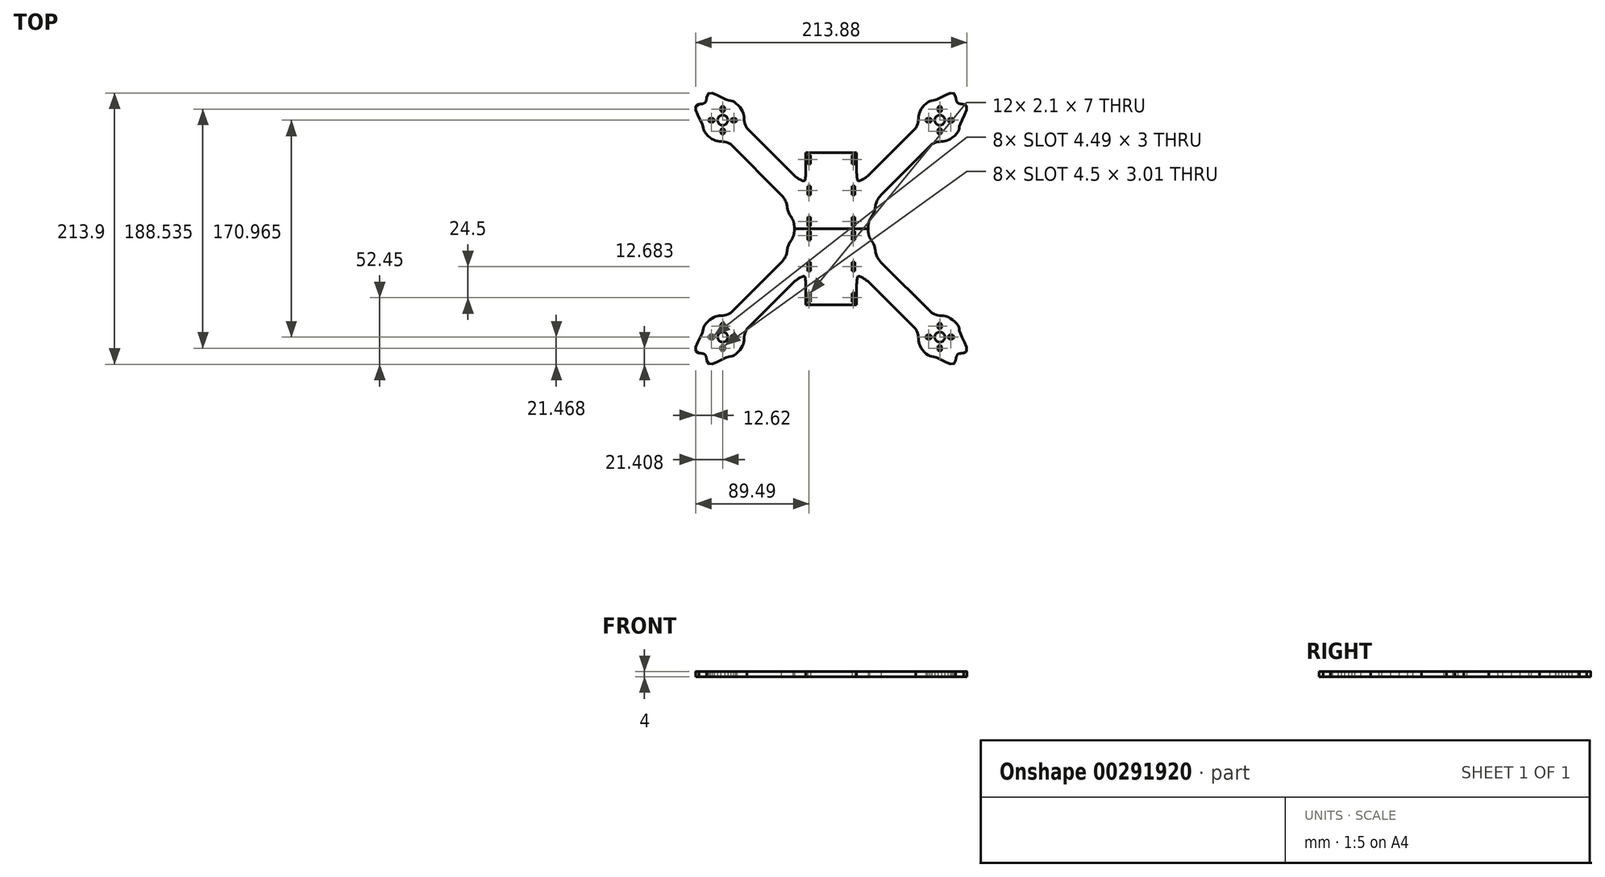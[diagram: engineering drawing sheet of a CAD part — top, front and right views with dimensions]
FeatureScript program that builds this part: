
annotation { "Feature Type Name" : "Feature", "Feature Type Description" : "" }
export const myFeature = defineFeature(function(context is Context, id is Id, definition is map)
    precondition{}
    {
        {
            var Q0;
            Q0=qCreatedBy(makeId("Top.planeOp"),FACE);
            var sketch = newSketch(context, id + "F0", { "sketchPlane" : qUnion([Q0])});
            skCircle(sketch, "E0", {"center": v(-85.5, 85.52) * mm, "radius": 4 * mm});
            skArc(sketch, "E1", {"start": v(-75.8, 84) * mm, "mid": v(-74.5, 85.58) * mm, "end": v(-76.01, 86.98) * mm});
            skLineSegment(sketch, "E2", {"start": v(-76.01, 86.98) * mm, "end": v(-77.51, 86.97) * mm});
            skLineSegment(sketch, "E3", {"start": v(-75.8, 84) * mm, "end": v(-77.3, 83.98) * mm});
            skArc(sketch, "E4", {"start": v(-77.51, 86.97) * mm, "mid": v(-79, 85.37) * mm, "end": v(-77.3, 83.98) * mm});
            skLineSegment(sketch, "E5", {"start": v(-85.53, 85.52) * mm, "end": v(-85.53, 96.52) * mm, "construction": true});
            skLineSegment(sketch, "E6", {"start": v(-85.5, 85.52) * mm, "end": v(-85.46, 74.52) * mm, "construction": true});
            skLineSegment(sketch, "E7.MirrorCS", {"start": v(-95.26, 84) * mm, "end": v(-93.76, 83.98) * mm});
            skLineSegment(sketch, "E8.MirrorCS", {"start": v(-95.06, 86.98) * mm, "end": v(-93.56, 86.97) * mm});
            skArc(sketch, "E9.MirrorCS", {"start": v(-93.56, 86.97) * mm, "mid": v(-92.07, 85.37) * mm, "end": v(-93.76, 83.98) * mm});
            skArc(sketch, "E10.MirrorCS", {"start": v(-95.26, 84) * mm, "mid": v(-96.57, 85.58) * mm, "end": v(-95.06, 86.98) * mm});
            skLineSegment(sketch, "E11", {"start": v(-96.57, 85.48) * mm, "end": v(-74.5, 85.56) * mm, "construction": true});
            skLineSegment(sketch, "E12.MirrorCS", {"start": v(-86.97, 77.51) * mm, "end": v(-86.97, 76.01) * mm});
            skLineSegment(sketch, "E13.MirrorCS", {"start": v(-83.97, 77.52) * mm, "end": v(-83.97, 76.02) * mm});
            skArc(sketch, "E14.MirrorCS", {"start": v(-83.97, 76.02) * mm, "mid": v(-85.46, 74.52) * mm, "end": v(-86.97, 76.01) * mm});
            skArc(sketch, "E15.MirrorCS", {"start": v(-86.97, 77.51) * mm, "mid": v(-85.48, 79.02) * mm, "end": v(-83.97, 77.52) * mm});
            skArc(sketch, "E16.MirrorCS", {"start": v(-87.03, 93.51) * mm, "mid": v(-85.52, 92.02) * mm, "end": v(-84.03, 93.52) * mm});
            skLineSegment(sketch, "E17.MirrorCS", {"start": v(-84.03, 93.52) * mm, "end": v(-84.03, 95.02) * mm});
            skLineSegment(sketch, "E18.MirrorCS", {"start": v(-87.03, 93.51) * mm, "end": v(-87.03, 95.01) * mm});
            skArc(sketch, "E19.MirrorCS", {"start": v(-84.03, 95.02) * mm, "mid": v(-85.54, 96.52) * mm, "end": v(-87.03, 95.01) * mm});
            skLineSegment(sketch, "E20", {"start": v(-85.5, 85.52) * mm, "end": v(-95.4, 95.42) * mm, "construction": true});
            skLineSegment(sketch, "E21", {"start": v(-85.53, 96.52) * mm, "end": v(-85.53, 99.52) * mm, "construction": true});
            skLineSegment(sketch, "E22", {"start": v(-96.57, 85.48) * mm, "end": v(-99.5, 85.48) * mm, "construction": true});
            skLineSegment(sketch, "E23", {"start": v(-85.46, 74.52) * mm, "end": v(-85.46, 71.52) * mm, "construction": true});
            skLineSegment(sketch, "E24", {"start": v(-85.5, 85.52) * mm, "end": v(-75.6, 95.42) * mm, "construction": true});
            skLineSegment(sketch, "E25", {"start": v(-85.5, 85.52) * mm, "end": v(-95.4, 75.62) * mm, "construction": true});
            skPoint(sketch, "E26", {"position": v(-56.32, 40.18) * mm});
            skLineSegment(sketch, "E27", {"start": v(-85.5, 85.52) * mm, "end": v(-75.6, 75.62) * mm, "construction": true});
            skCircle(sketch, "E28", {"center": v(-85.5, 85.52) * mm, "radius": 14 * mm, "construction": true});
            skLineSegment(sketch, "E29", {"start": v(-74.5, 85.56) * mm, "end": v(-71.5, 85.56) * mm, "construction": true});
            skPoint(sketch, "E30.visualSharp", {"position": v(-85.46, 71.52) * mm});
            skPoint(sketch, "E31.visualSharp", {"position": v(-71.5, 85.56) * mm});
            skLineSegment(sketch, "E32", {"start": v(-20, 60) * mm, "end": v(0, 60) * mm});
            skLineSegment(sketch, "E33", {"start": v(0, 60) * mm, "end": v(0, 0) * mm});
            skLineSegment(sketch, "E34", {"start": v(-85.5, 85.52) * mm, "end": v(-22, 85.52) * mm, "construction": true});
            skCircle(sketch, "E35", {"center": v(-85.5, 85.52) * mm, "radius": 63.5 * mm, "construction": true});
            skLineSegment(sketch, "E36", {"start": v(-29, -0.02) * mm, "end": v(-29, 0) * mm, "construction": true});
            skPoint(sketch, "E37.visualSharp", {"position": v(-86.14, 109.55) * mm});
            skPoint(sketch, "E38.visualSharp", {"position": v(-109.53, 84.88) * mm});
            skArc(sketch, "E39", {"start": v(-29, 0) * mm, "mid": v(-29.3, 3.46) * mm, "end": v(-30.18, 6.81) * mm});
            skLineSegment(sketch, "E40.trimOffspring", {"start": v(-20.02, -0.02) * mm, "end": v(-20, 0) * mm});
            skLineSegment(sketch, "E41", {"start": v(-66.5, 79.25) * mm, "end": v(-29.98, 42.73) * mm});
            skLineSegment(sketch, "E42", {"start": v(-79.23, 66.52) * mm, "end": v(-39.33, 26.61) * mm});
            skFitSpline(sketch, "E43", {"points": [v(-79.23, 66.52) * mm, v(-84.99, 68.53) * mm, v(-89.4, 68.97) * mm, v(-94.25, 70.94) * mm, v(-100.14, 76.88) * mm, v(-102.47, 84.44) * mm, v(-97.84, 97.21) * mm], "startDerivative": vector(-52.25, 30.78) * mm, "endDerivative": vector(200.56, -55.38) * mm});
            skFitSpline(sketch, "E44.MirrorCS", {"points": [v(-66.5, 79.25) * mm, v(-68.5, 85) * mm, v(-68.95, 89.42) * mm, v(-70.93, 94.27) * mm, v(-76.86, 100.16) * mm, v(-84.42, 102.48) * mm, v(-97.2, 97.85) * mm], "startDerivative": vector(-30.78, 52.25) * mm, "endDerivative": vector(55.38, -200.56) * mm});
            skFitSpline(sketch, "E45", {"points": [v(-39.33, 26.61) * mm, v(-33.76, 13.03) * mm, v(-29, 0) * mm], "startDerivative": vector(33.41, -38.03) * mm, "endDerivative": vector(-8.78, -30.15) * mm});
            skPoint(sketch, "E46.orphan", {"position": v(-104.03, 90.68) * mm});
            skPoint(sketch, "E37.filletArc.end.orphan", {"position": v(-91.65, 103.74) * mm});
            skPoint(sketch, "E47.end.orphan", {"position": v(-20, 46.85) * mm});
            skFitSpline(sketch, "E48", {"points": [v(-30.19, 42.93) * mm, v(-21.98, 37.6) * mm, v(-20, 44.2) * mm], "startDerivative": vector(14.75, -14.96) * mm, "endDerivative": vector(2.34, 37.6) * mm});
            skLineSegment(sketch, "E49.trimOffspring", {"start": v(-20, 44.2) * mm, "end": v(-20, 60) * mm});
            skFitSpline(sketch, "E50", {"points": [v(-98.1, 103.81) * mm, v(-99.54, 99.28) * mm, v(-104.27, 98.07) * mm], "startDerivative": vector(-1.03, -9.76) * mm, "endDerivative": vector(-11.13, -1.87) * mm});
            skLineSegment(sketch, "E51", {"start": v(-29, 0) * mm, "end": v(0, 0) * mm});
            skLineSegment(sketch, "E52.bottom", {"start": v(-18.5, 58) * mm, "end": v(-16.4, 58) * mm});
            skLineSegment(sketch, "E52.top", {"start": v(-18.5, 51) * mm, "end": v(-16.4, 51) * mm});
            skLineSegment(sketch, "E52.left", {"start": v(-18.5, 58) * mm, "end": v(-18.5, 51) * mm});
            skLineSegment(sketch, "E52.right", {"start": v(-16.4, 58) * mm, "end": v(-16.4, 51) * mm});
            skLineSegment(sketch, "E53.bottom", {"start": v(-18.5, 33.5) * mm, "end": v(-16.4, 33.5) * mm});
            skLineSegment(sketch, "E53.top", {"start": v(-18.5, 26.5) * mm, "end": v(-16.4, 26.5) * mm});
            skLineSegment(sketch, "E53.left", {"start": v(-18.5, 33.5) * mm, "end": v(-18.5, 26.5) * mm});
            skLineSegment(sketch, "E53.right", {"start": v(-16.4, 33.5) * mm, "end": v(-16.4, 26.5) * mm});
            skLineSegment(sketch, "E54.bottom", {"start": v(-18.5, 9) * mm, "end": v(-16.4, 9) * mm});
            skLineSegment(sketch, "E54.top", {"start": v(-18.5, 2) * mm, "end": v(-16.4, 2) * mm});
            skLineSegment(sketch, "E54.left", {"start": v(-18.5, 9) * mm, "end": v(-18.5, 2) * mm});
            skLineSegment(sketch, "E54.right", {"start": v(-16.4, 9) * mm, "end": v(-16.4, 2) * mm});
            skLineSegment(sketch, "E55", {"start": v(-18.5, 51) * mm, "end": v(-18.5, 0) * mm, "construction": true});
            skLineSegment(sketch, "E56", {"start": v(-16.4, 9) * mm, "end": v(-16.4, 26.5) * mm, "construction": true});
            skLineSegment(sketch, "E57", {"start": v(-16.4, 33.5) * mm, "end": v(-16.4, 51) * mm, "construction": true});
            skSolve(sketch);
        }
        {
            var Q0;
            Q0 = qSketchRegion(id + "F0", true);
            extrude(context, id + "F1", {"entities" : qUnion([Q0]), "depth" : 4 * mm});
        }
        {
            var Q0;
            Q0=makeQuery(id+"F1.opExtrude","SWEPT_BODY",BODY,{"disambiguationData":[OSD([sQuery(id+"F0.wireOp",EDGE,"E0"),sQuery(id+"F0.wireOp",EDGE,"E1"),sQuery(id+"F0.wireOp",EDGE,"E2"),sQuery(id+"F0.wireOp",EDGE,"E3"),sQuery(id+"F0.wireOp",EDGE,"E4"),sQuery(id+"F0.wireOp",EDGE,"E7.MirrorCS"),sQuery(id+"F0.wireOp",EDGE,"E8.MirrorCS"),sQuery(id+"F0.wireOp",EDGE,"E9.MirrorCS"),sQuery(id+"F0.wireOp",EDGE,"E10.MirrorCS"),sQuery(id+"F0.wireOp",EDGE,"E12.MirrorCS"),sQuery(id+"F0.wireOp",EDGE,"E13.MirrorCS"),sQuery(id+"F0.wireOp",EDGE,"E14.MirrorCS"),sQuery(id+"F0.wireOp",EDGE,"E15.MirrorCS"),sQuery(id+"F0.wireOp",EDGE,"E16.MirrorCS"),sQuery(id+"F0.wireOp",EDGE,"E17.MirrorCS"),sQuery(id+"F0.wireOp",EDGE,"E18.MirrorCS"),sQuery(id+"F0.wireOp",EDGE,"E19.MirrorCS"),sQuery(id+"F0.wireOp",EDGE,"E32"),sQuery(id+"F0.wireOp",EDGE,"E33"),sQuery(id+"F0.wireOp",EDGE,"E39"),sQuery(id+"F0.wireOp",EDGE,"E41"),sQuery(id+"F0.wireOp",EDGE,"E42"),sQuery(id+"F0.wireOp",EDGE,"E43"),sQuery(id+"F0.wireOp",EDGE,"E44.MirrorCS"),sQuery(id+"F0.wireOp",EDGE,"E45"),sQuery(id+"F0.wireOp",EDGE,"E48"),sQuery(id+"F0.wireOp",EDGE,"E49.trimOffspring"),sQuery(id+"F0.wireOp",EDGE,"E50"),sQuery(id+"F0.wireOp",EDGE,"Sy01u6gg-gxzx-yRzi-Doui-YO7uCB7MVHyv")])]});
            var Q1;
            Q1=qCreatedBy(makeId("Right.planeOp"),FACE);
            mirror(context, id + "F2", {"operationType" : NewBodyOperationType.ADD, "entities" : qUnion([Q0]), "mirrorPlane" : qUnion([Q1])});
        }
        {
            var Q0;
            Q0=makeQuery(id+"F1.opExtrude","SWEPT_BODY",BODY,{"disambiguationData":[OSD([sQuery(id+"F0.wireOp",EDGE,"E0"),sQuery(id+"F0.wireOp",EDGE,"E1"),sQuery(id+"F0.wireOp",EDGE,"E2"),sQuery(id+"F0.wireOp",EDGE,"E3"),sQuery(id+"F0.wireOp",EDGE,"E4"),sQuery(id+"F0.wireOp",EDGE,"E7.MirrorCS"),sQuery(id+"F0.wireOp",EDGE,"E8.MirrorCS"),sQuery(id+"F0.wireOp",EDGE,"E9.MirrorCS"),sQuery(id+"F0.wireOp",EDGE,"E10.MirrorCS"),sQuery(id+"F0.wireOp",EDGE,"E12.MirrorCS"),sQuery(id+"F0.wireOp",EDGE,"E13.MirrorCS"),sQuery(id+"F0.wireOp",EDGE,"E14.MirrorCS"),sQuery(id+"F0.wireOp",EDGE,"E15.MirrorCS"),sQuery(id+"F0.wireOp",EDGE,"E16.MirrorCS"),sQuery(id+"F0.wireOp",EDGE,"E17.MirrorCS"),sQuery(id+"F0.wireOp",EDGE,"E18.MirrorCS"),sQuery(id+"F0.wireOp",EDGE,"E19.MirrorCS"),sQuery(id+"F0.wireOp",EDGE,"E32"),sQuery(id+"F0.wireOp",EDGE,"E33"),sQuery(id+"F0.wireOp",EDGE,"E39"),sQuery(id+"F0.wireOp",EDGE,"E41"),sQuery(id+"F0.wireOp",EDGE,"E42"),sQuery(id+"F0.wireOp",EDGE,"E43"),sQuery(id+"F0.wireOp",EDGE,"E44.MirrorCS"),sQuery(id+"F0.wireOp",EDGE,"E45"),sQuery(id+"F0.wireOp",EDGE,"E48"),sQuery(id+"F0.wireOp",EDGE,"E49.trimOffspring"),sQuery(id+"F0.wireOp",EDGE,"E50"),sQuery(id+"F0.wireOp",EDGE,"Sy01u6gg-gxzx-yRzi-Doui-YO7uCB7MVHyv")])]});
            var Q1;
            Q1=qCreatedBy(makeId("Front.planeOp"),FACE);
            mirror(context, id + "F3", {"entities" : qUnion([Q0]), "mirrorPlane" : qUnion([Q1])});
        }
    });
